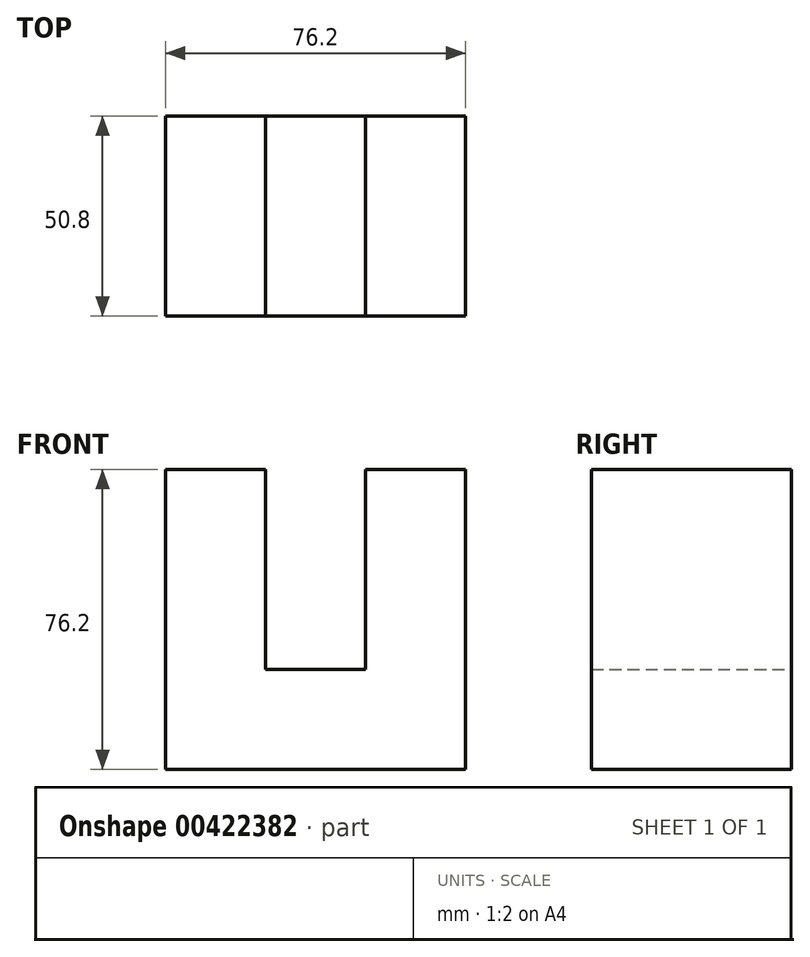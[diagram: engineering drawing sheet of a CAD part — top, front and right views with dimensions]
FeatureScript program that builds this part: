
annotation { "Feature Type Name" : "Feature", "Feature Type Description" : "" }
export const myFeature = defineFeature(function(context is Context, id is Id, definition is map)
    precondition{}
    {
        {
            var Q0;
            Q0=qCreatedBy(makeId("Front.planeOp"),FACE);
            var sketch = newSketch(context, id + "F0", { "sketchPlane" : qUnion([Q0])});
            skLineSegment(sketch, "E0", {"start": v(-50.8, 39.39) * mm, "end": v(-50.8, -36.81) * mm});
            skLineSegment(sketch, "E1", {"start": v(-50.8, -36.81) * mm, "end": v(25.4, -36.81) * mm});
            skLineSegment(sketch, "E2", {"start": v(25.4, -36.81) * mm, "end": v(25.4, 39.39) * mm});
            skLineSegment(sketch, "E3", {"start": v(25.4, 39.39) * mm, "end": v(0, 39.39) * mm});
            skLineSegment(sketch, "E4", {"start": v(0, 39.39) * mm, "end": v(0, -11.41) * mm});
            skLineSegment(sketch, "E5", {"start": v(0, -11.41) * mm, "end": v(-25.4, -11.41) * mm});
            skLineSegment(sketch, "E6", {"start": v(-25.4, -11.41) * mm, "end": v(-25.4, 39.39) * mm});
            skLineSegment(sketch, "E7", {"start": v(-25.4, 39.39) * mm, "end": v(-50.8, 39.39) * mm});
            skSolve(sketch);
        }
        {
            var Q0;
            Q0=makeQuery(id+"F0.imprint","IMPRINT",FACE,{"disambiguationData":[TD([[makeQuery(id+"F0.imprint","IMPRINT",EDGE,{"derivedFrom":sQuery(id+"F0.wireOp",EDGE,"E0")}),1.0]])]});
            extrude(context, id + "F1", {"entities" : qUnion([Q0]), "depth" : 50.8 * mm});
        }
    });
